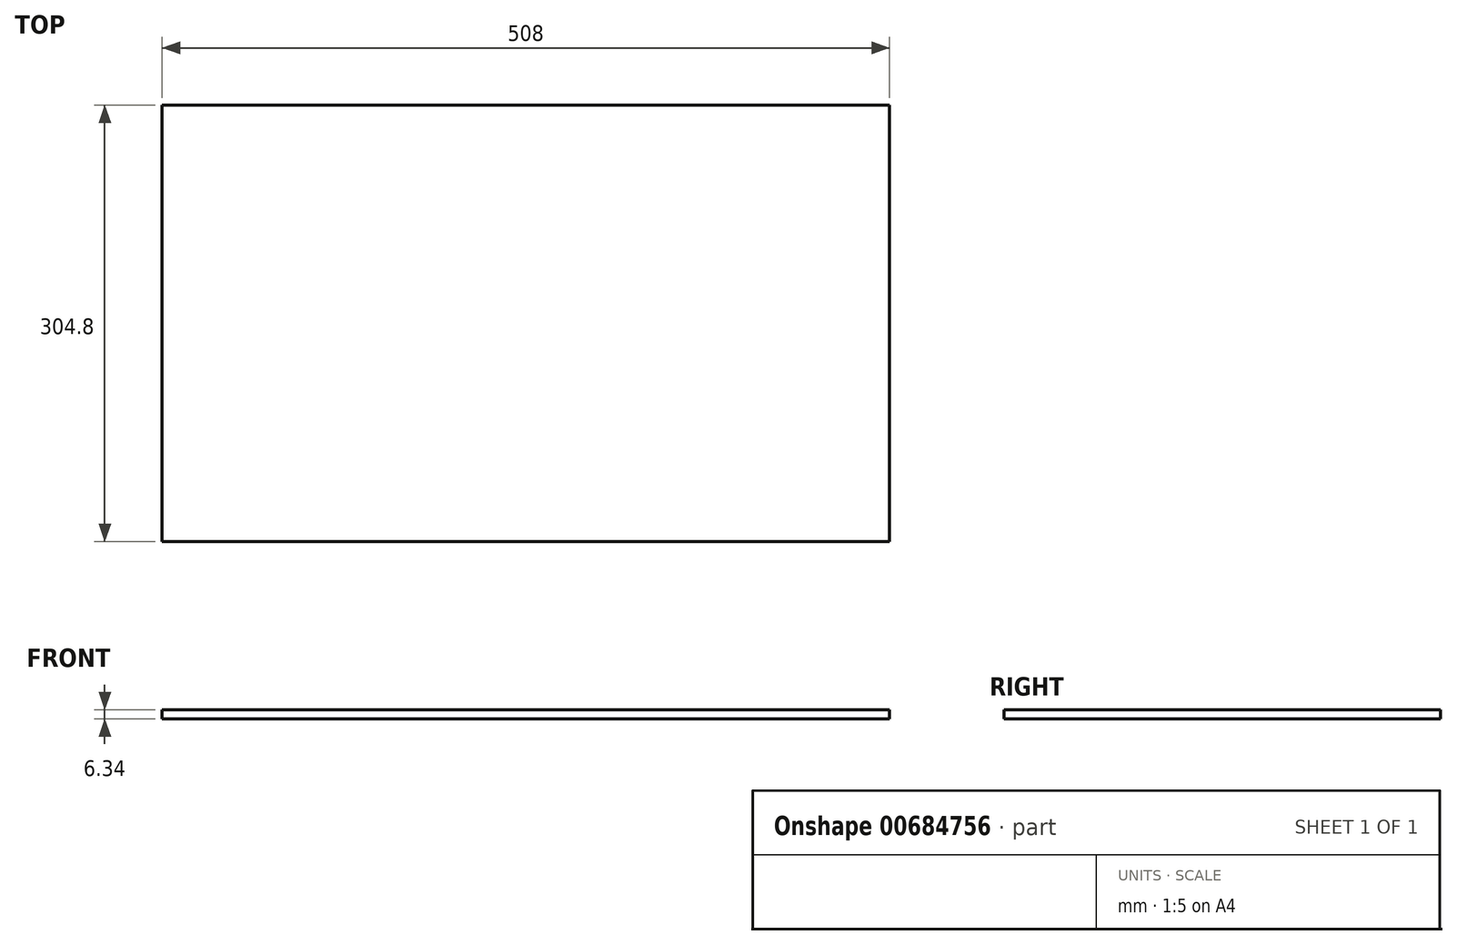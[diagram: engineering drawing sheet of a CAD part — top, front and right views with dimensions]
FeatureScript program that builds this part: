
annotation { "Feature Type Name" : "Feature", "Feature Type Description" : "" }
export const myFeature = defineFeature(function(context is Context, id is Id, definition is map)
    precondition{}
    {
        {
            var Q0;
            Q0=qCreatedBy(makeId("Front.planeOp"),FACE);
            var sketch = newSketch(context, id + "F0", { "sketchPlane" : qUnion([Q0])});
            skLineSegment(sketch, "E0.bottom", {"start": v(-254, 3.17) * mm, "end": v(254, 3.17) * mm});
            skLineSegment(sketch, "E0.top", {"start": v(-254, -3.18) * mm, "end": v(254, -3.18) * mm});
            skLineSegment(sketch, "E0.left", {"start": v(-254, 3.18) * mm, "end": v(-254, -3.18) * mm});
            skLineSegment(sketch, "E0.right", {"start": v(254, 3.18) * mm, "end": v(254, -3.18) * mm});
            skLineSegment(sketch, "E1", {"start": v(-254, 3.17) * mm, "end": v(254, -3.17) * mm, "construction": true});
            skSolve(sketch);
        }
        {
            var Q0;
            Q0=qSketchRegion(id+"F0",true);
            extrude(context, id + "F1", {"entities" : qUnion([Q0]), "endBound" : BoundingType.SYMMETRIC, "depth" : 304.8 * mm, "offsetDistance" : 25.4 * mm});
        }
    });
